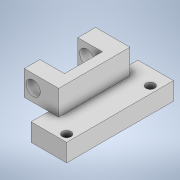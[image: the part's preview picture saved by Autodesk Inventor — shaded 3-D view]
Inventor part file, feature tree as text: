
AUTODESK INVENTOR PART (.ipt)
format: ipt  version: 2022.1 (Build 261234020, 234B)  size: 312,832 bytes
history: native  units: mm
features: extrude x6, sketch x6
ambient origin geometry x8: Origin, YZ Plane, XZ Plane, XY Plane, X Axis, Y Axis, Z Axis, Center Point
bodies: Solid1 (feature_tree)
feature tree (12):
  extrude  "Extrusion1"  Depth=10.0mm
  extrude  "Extrusion2"  Depth=5.0mm
  extrude  "Extrusion3"  Depth=23.496521mm
  extrude  "Extrusion4"  Depth=2.0mm
  extrude  "Extrusion5"  Depth=20.0mm
  extrude  "Extrusion6"  Depth=5.0mm
  sketch  "Sketch1"  dims[d0=30.0mm d1=10.0mm]
  sketch  "Sketch2"  dims[d2=5.0mm d3=0.0mm d4=2.5mm]
  sketch  "Sketch3"  dims[d5=2.5mm d6=23.496521mm]
  sketch  "Sketch4"  dims[d7=2.0mm d8=2.0mm]
  sketch  "Sketch5"  dims[d9=0.0mm d10=0.0mm d11=20.0mm]
  sketch  "Sketch6"  dims[d12=7.0mm d13=0.0mm d14=4.0mm d15=2.5mm d16=0.0mm d17=0.0mm d18=9.25mm d19=5.0mm d20=10.0mm d21=0.0mm d22=5.0mm d23=0.0mm d24=0.0mm]
